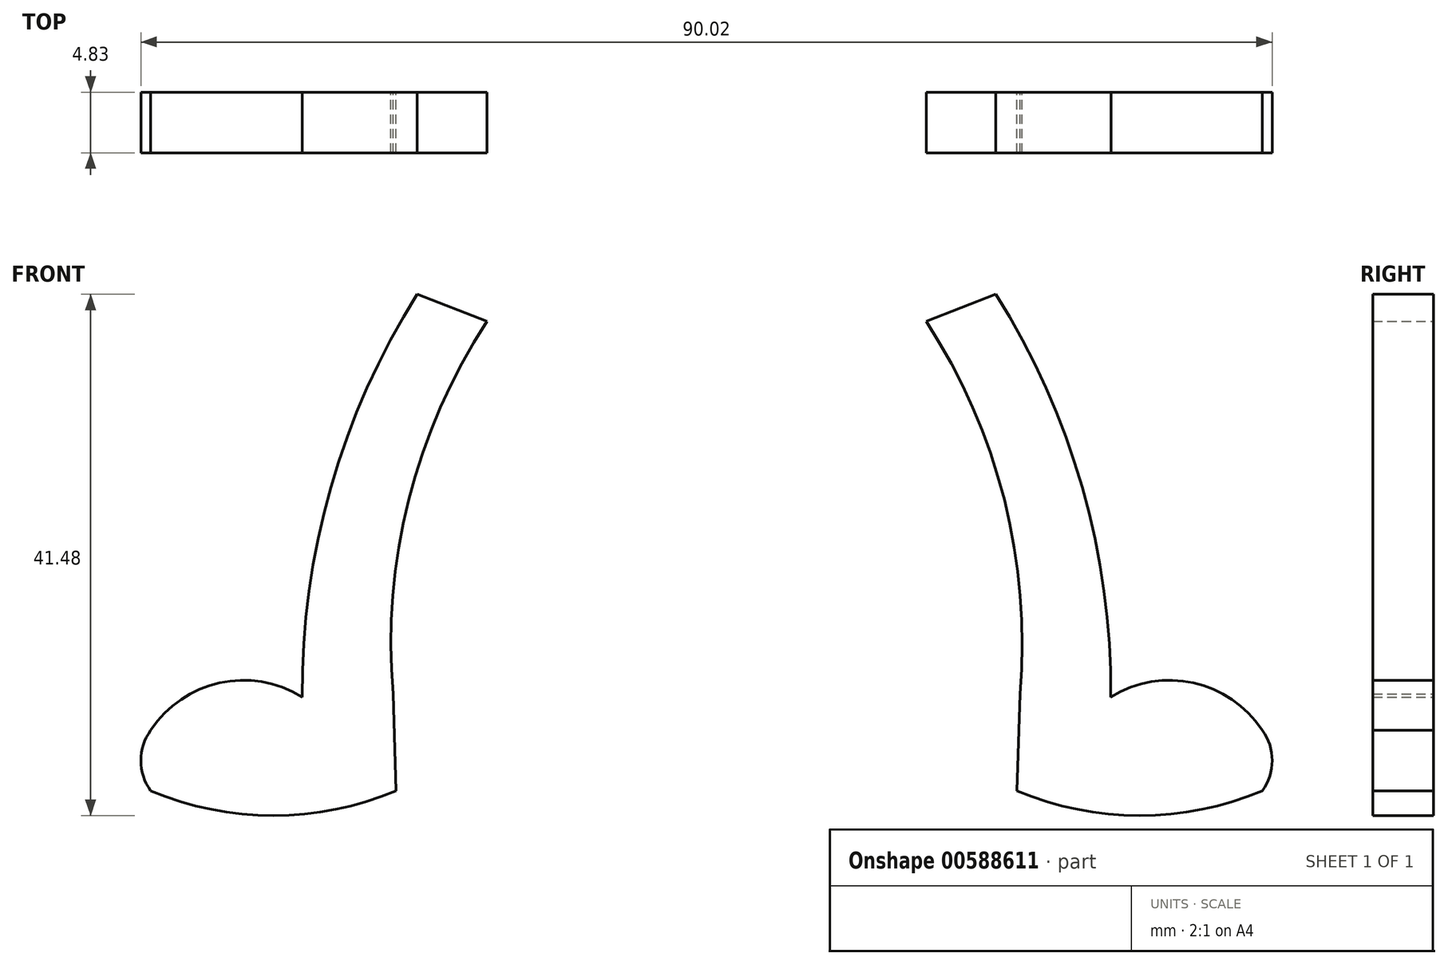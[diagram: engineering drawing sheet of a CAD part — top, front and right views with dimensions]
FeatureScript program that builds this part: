
annotation { "Feature Type Name" : "Feature", "Feature Type Description" : "" }
export const myFeature = defineFeature(function(context is Context, id is Id, definition is map)
    precondition{}
    {
        {
            var Q0;
            Q0=qCreatedBy(makeId("Front.planeOp"),FACE);
            var sketch = newSketch(context, id + "F0", { "sketchPlane" : qUnion([Q0])});
            skArc(sketch, "E0", {"start": v(32.17, -43.02) * mm, "mid": v(29.9, -26.33) * mm, "end": v(23.01, -10.97) * mm});
            skArc(sketch, "E1", {"start": v(24.94, -42.78) * mm, "mid": v(23.7, -27.33) * mm, "end": v(17.47, -13.13) * mm});
            skArc(sketch, "E2", {"start": v(44.22, -45.67) * mm, "mid": v(38.74, -41.9) * mm, "end": v(32.17, -43.02) * mm});
            skArc(sketch, "E3", {"start": v(44.22, -50.49) * mm, "mid": v(45, -48.08) * mm, "end": v(44.22, -45.67) * mm});
            skArc(sketch, "E4", {"start": v(24.7, -50.49) * mm, "mid": v(34.46, -52.45) * mm, "end": v(44.22, -50.49) * mm});
            skLineSegment(sketch, "E5", {"start": v(24.94, -42.78) * mm, "end": v(24.7, -50.49) * mm});
            skLineSegment(sketch, "E6", {"start": v(24.94, -42.78) * mm, "end": v(32.17, -43.02) * mm});
            skLineSegment(sketch, "E7", {"start": v(17.47, -13.13) * mm, "end": v(23.01, -10.97) * mm});
            skLineSegment(sketch, "E8.MirrorCS", {"start": v(-17.47, -13.13) * mm, "end": v(-23.01, -10.97) * mm});
            skArc(sketch, "E9.MirrorCS", {"start": v(-24.94, -42.78) * mm, "mid": v(-23.7, -27.33) * mm, "end": v(-17.47, -13.13) * mm});
            skArc(sketch, "E10.MirrorCS", {"start": v(-32.17, -43.02) * mm, "mid": v(-29.9, -26.33) * mm, "end": v(-23.01, -10.97) * mm});
            skLineSegment(sketch, "E11.MirrorCS", {"start": v(-24.94, -42.78) * mm, "end": v(-32.17, -43.02) * mm});
            skLineSegment(sketch, "E12.MirrorCS", {"start": v(-24.94, -42.78) * mm, "end": v(-24.7, -50.49) * mm});
            skArc(sketch, "E13.MirrorCS", {"start": v(-24.7, -50.49) * mm, "mid": v(-34.46, -52.45) * mm, "end": v(-44.22, -50.49) * mm});
            skArc(sketch, "E14.MirrorCS", {"start": v(-44.22, -45.67) * mm, "mid": v(-38.74, -41.9) * mm, "end": v(-32.17, -43.02) * mm});
            skArc(sketch, "E15.MirrorCS", {"start": v(-44.22, -50.49) * mm, "mid": v(-45, -48.08) * mm, "end": v(-44.22, -45.67) * mm});
            skSolve(sketch);
        }
        {
            var Q0;
            Q0 = qSketchRegion(id + "F0", true);
            extrude(context, id + "F1", {"entities" : qUnion([Q0]), "depth" : 4.83 * mm, "offsetDistance" : 25.4 * mm});
        }
    });
